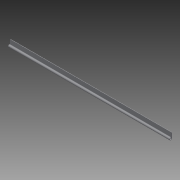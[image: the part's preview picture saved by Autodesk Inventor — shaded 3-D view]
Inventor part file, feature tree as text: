
AUTODESK INVENTOR PART (.ipt)
format: ipt  version: 2015 SP1 (Build 190203100, 203)  size: 164,352 bytes
history: native  units: in
note: dims shown in document units (in); Inventor stores cm internally (conversion verified against a paired STEP export)
features: sketch x4, extrude x3, pattern_linear x2, hole x1
ambient origin geometry x8: Origin, YZ Plane, XZ Plane, XY Plane, X Axis, Y Axis, Z Axis, Center Point
bodies: Solid1 (feature_tree)
feature tree (10):
  extrude  "Extrusion1"  Depth=0.0625in
  extrude  "Extrusion2"  Depth=0.1875in
  extrude  "Extrusion3"  Depth=25.0in TaperAngle=0.0deg
  pattern_linear  "Rectangular Pattern1"  Spacing1=25.0in  [1 undecoded]
  hole  "Hole1"  [1 undecoded]
  pattern_linear  "Rectangular Pattern2"  Count1=13 Spacing1=2.0in
  sketch  "Sketch1"  dims[d0=1.0in d1=0.0625in]
  sketch  "Sketch2"  dims[d2=0.375in d3=0.1875in]
  sketch  "Sketch3"  dims[d4=0.125in d5=25.0in d6=0.0in]
  sketch  "Sketch4"  dims[d7=0.25in d8=25.0in d9=0.0in d10=1.0in d11=0.0in d12=5.1181in d14=2.0in d15=0.375in d16=0.5in d17=0.25in d18=0.75in d19=0.375in d20=0.25in d21=0.5635in d22=1.0in d23=0.8108in d24=9.8425in d26=1.0in]
note: 2 required parameter values undecoded (feature->parameter linkage not recoverable at this tier; creation-order binding heuristic only, values carry confidence <= 0.55)
